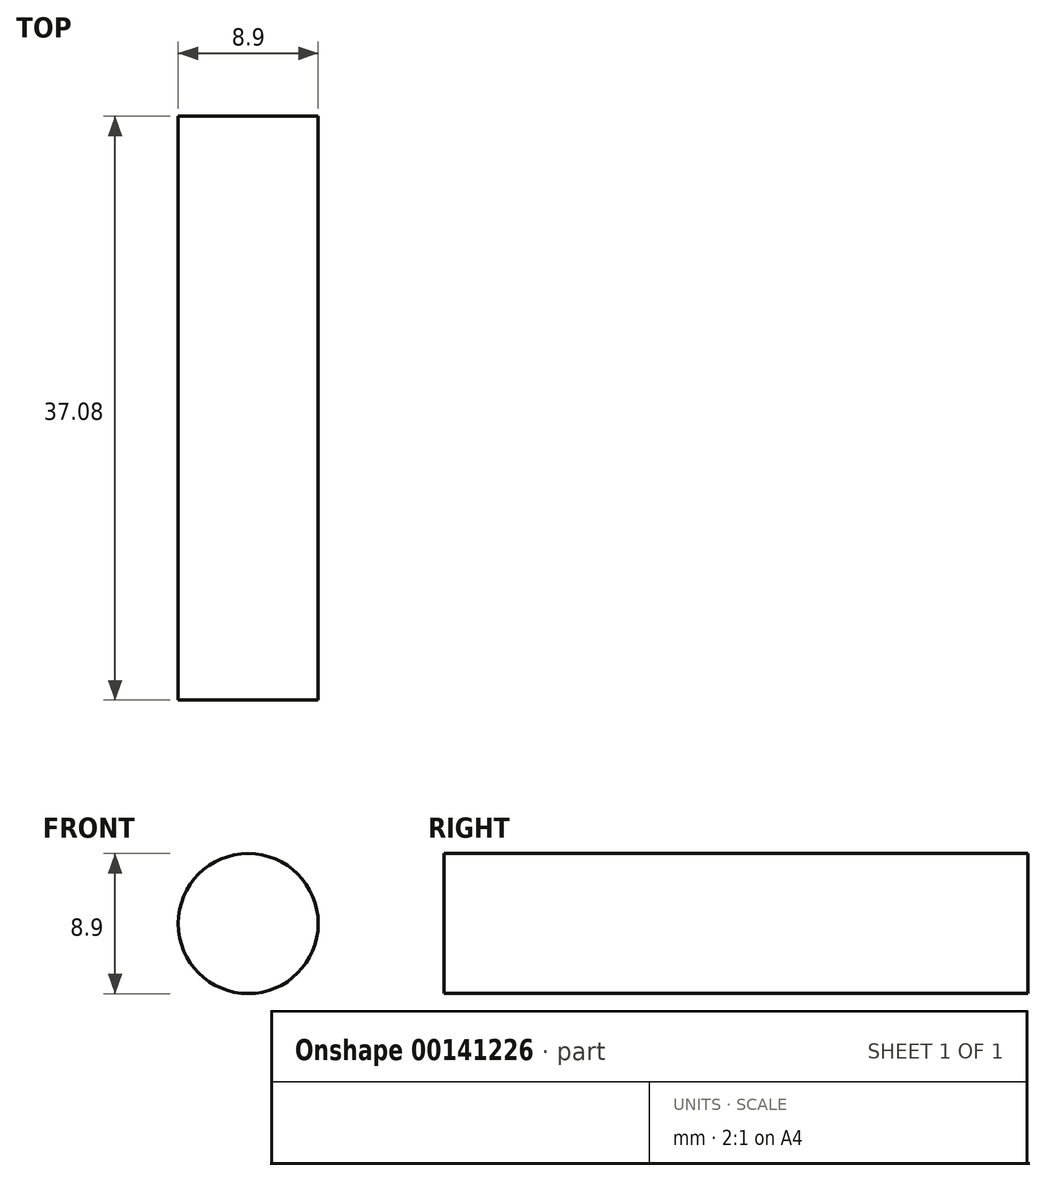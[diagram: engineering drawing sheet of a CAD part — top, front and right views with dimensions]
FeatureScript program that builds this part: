
annotation { "Feature Type Name" : "Feature", "Feature Type Description" : "" }
export const myFeature = defineFeature(function(context is Context, id is Id, definition is map)
    precondition{}
    {
        {
            var Q0;
            Q0=qCreatedBy(makeId("Front.planeOp"),FACE);
            var sketch = newSketch(context, id + "F0", { "sketchPlane" : qUnion([Q0])});
            skCircle(sketch, "E0", {"center": v(0, 0) * mm, "radius": 4.45 * mm});
            skSolve(sketch);
        }
        {
            var Q0;
            Q0 = qSketchRegion(id + "F0", true);
            extrude(context, id + "F1", {"entities" : qUnion([Q0]), "depth" : 37.08 * mm});
        }
    });
